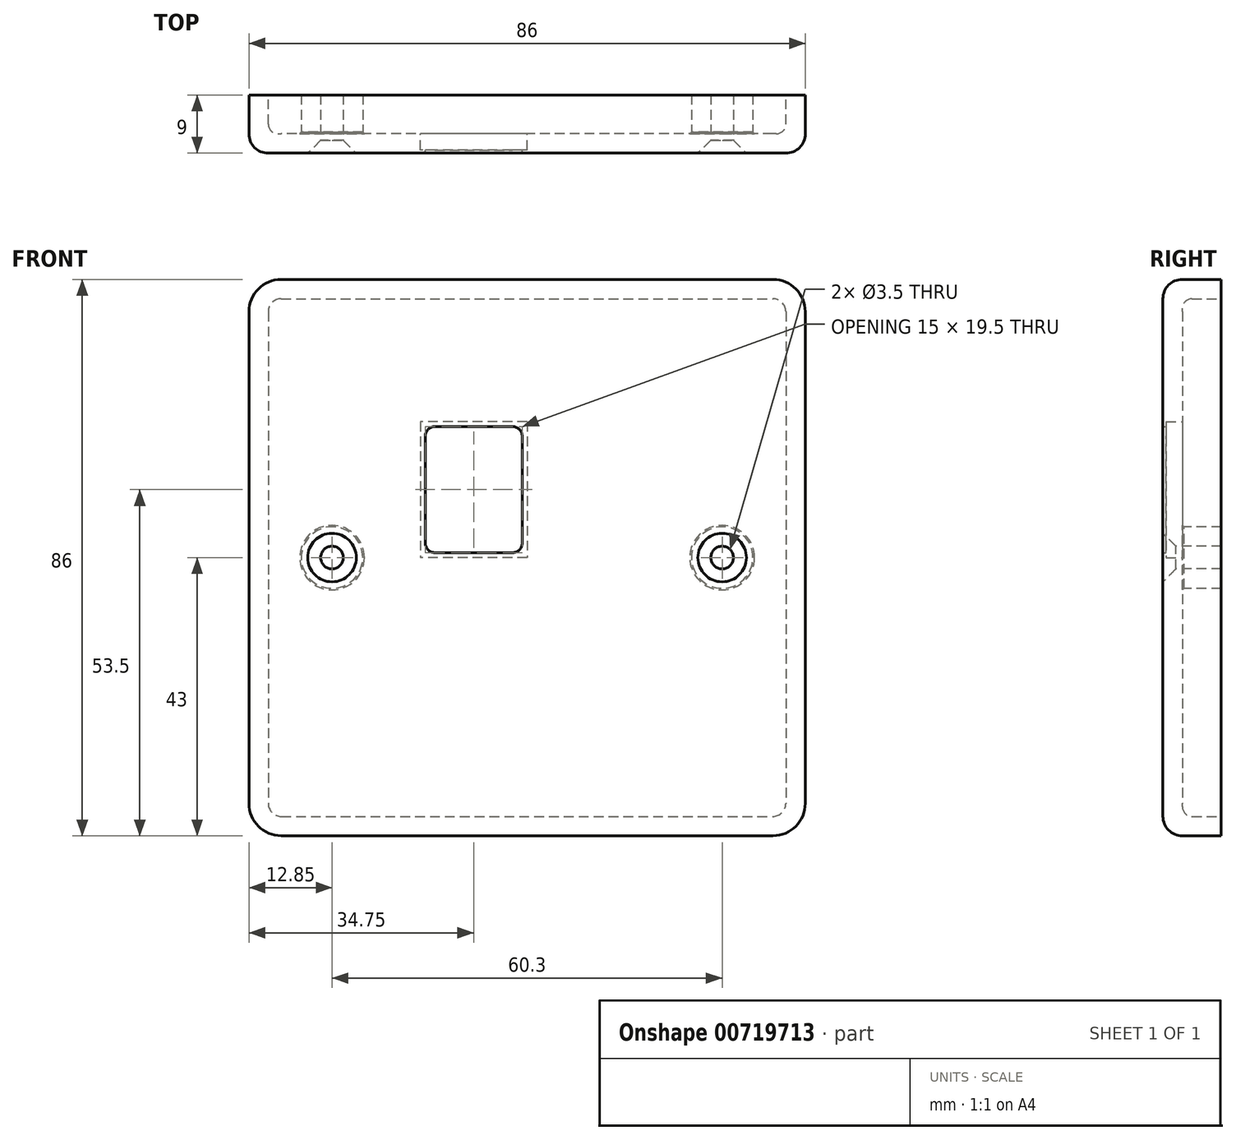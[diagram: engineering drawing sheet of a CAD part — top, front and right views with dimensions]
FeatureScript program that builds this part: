
annotation { "Feature Type Name" : "Feature", "Feature Type Description" : "" }
export const myFeature = defineFeature(function(context is Context, id is Id, definition is map)
    precondition{}
    {
        {
            var Q0;
            Q0=qCreatedBy(makeId("Front.planeOp"),FACE);
            var sketch = newSketch(context, id + "F0", { "sketchPlane" : qUnion([Q0])});
            skLineSegment(sketch, "E0.bottom", {"start": v(-43, 43) * mm, "end": v(43, 43) * mm});
            skLineSegment(sketch, "E0.top", {"start": v(-43, -43) * mm, "end": v(43, -43) * mm});
            skLineSegment(sketch, "E0.left", {"start": v(-43, 43) * mm, "end": v(-43, -43) * mm});
            skLineSegment(sketch, "E0.right", {"start": v(43, 43) * mm, "end": v(43, -43) * mm});
            skPoint(sketch, "E0.middle", {"position": v(0, 0) * mm});
            skSolve(sketch);
        }
        {
            var Q0;
            Q0 = qSketchRegion(id + "F0", true);
            extrude(context, id + "F1", {"entities" : qUnion([Q0]), "depth" : 9 * mm, "offsetDistance" : 25 * mm});
        }
        {
            var Q0;
            Q0=makeQuery(id+"F1.opExtrude","SWEPT_EDGE",EDGE,{"disambiguationData":[OSD([sQuery(id+"F0.wireOp",EDGE,"E0.bottom"),sQuery(id+"F0.wireOp",EDGE,"E0.left")])]});
            var Q1;
            Q1=makeQuery(id+"F1.opExtrude","SWEPT_EDGE",EDGE,{"disambiguationData":[OSD([sQuery(id+"F0.wireOp",EDGE,"E0.bottom"),sQuery(id+"F0.wireOp",EDGE,"E0.right")])]});
            var Q2;
            Q2=makeQuery(id+"F1.opExtrude","SWEPT_EDGE",EDGE,{"disambiguationData":[OSD([sQuery(id+"F0.wireOp",EDGE,"E0.top"),sQuery(id+"F0.wireOp",EDGE,"E0.right")])]});
            var Q3;
            Q3=makeQuery(id+"F1.opExtrude","SWEPT_EDGE",EDGE,{"disambiguationData":[OSD([sQuery(id+"F0.wireOp",EDGE,"E0.top"),sQuery(id+"F0.wireOp",EDGE,"E0.left")])]});
            fillet(context, id + "F2", {"entities" : qUnion([Q0, Q1, Q2, Q3]), "radius" : 5 * mm, "tangentPropagation" : true, "allowEdgeOverflow" : false});
        }
        {
            var Q0;
            Q0=makeQuery(id+"F1.opExtrude","CAP_EDGE",EDGE,{"disambiguationData":[OSD([sQuery(id+"F0.wireOp",EDGE,"E0.right")])],"isStart":false});
            fillet(context, id + "F3", {"entities" : qUnion([Q0]), "radius" : 3 * mm, "tangentPropagation" : true, "allowEdgeOverflow" : false});
        }
        {
            var Q0;
            Q0=makeQuery(id+"F1.opExtrude","CAP_FACE",FACE,{"disambiguationData":[OSD([sQuery(id+"F0.wireOp",EDGE,"E0.bottom"),sQuery(id+"F0.wireOp",EDGE,"E0.top"),sQuery(id+"F0.wireOp",EDGE,"E0.left"),sQuery(id+"F0.wireOp",EDGE,"E0.right")])],"isStart":false});
            var sketch = newSketch(context, id + "F4", { "sketchPlane" : qUnion([Q0])});
            skPoint(sketch, "E1", {"position": v(-30.15, 0) * mm});
            skPoint(sketch, "E2", {"position": v(30.15, 0) * mm});
            skSolve(sketch);
        }
        {
            var Q0;
            Q0=sQuery(id+"F4.wireOp",VERTEX,"E1");
            var Q1;
            Q1=sQuery(id+"F4.wireOp",VERTEX,"E2");
            var Q2;
            Q2=makeQuery(id+"F1.opExtrude","SWEPT_BODY",BODY,{"disambiguationData":[OSD([sQuery(id+"F0.wireOp",EDGE,"E0.bottom"),sQuery(id+"F0.wireOp",EDGE,"E0.top"),sQuery(id+"F0.wireOp",EDGE,"E0.left"),sQuery(id+"F0.wireOp",EDGE,"E0.right")])]});
            hole(context, id + "F5", {"style" : HoleStyle.C_SINK, "endStyle" : HoleEndStyle.THROUGH, "holeDiameter" : 3.5 * mm, "cSinkDiameter" : 7.5 * mm, "cSinkAngle" : 90 * degree, "majorDiameter" : 5 * mm, "isTappedThrough" : true, "tappedDepth" : 12 * mm, "tapClearance" : 3, "locations" : qUnion([Q0, Q1]), "scope" : qUnion([Q2])});
        }
        {
            var Q0;
            Q0=makeQuery(id+"F1.opExtrude","CAP_FACE",FACE,{"disambiguationData":[OSD([sQuery(id+"F0.wireOp",EDGE,"E0.bottom"),sQuery(id+"F0.wireOp",EDGE,"E0.top"),sQuery(id+"F0.wireOp",EDGE,"E0.left"),sQuery(id+"F0.wireOp",EDGE,"E0.right")])],"isStart":true});
            shell(context, id + "F6", {"entities" : qUnion([Q0]), "thickness" : 3 * mm});
        }
        {
            var Q0;
            {var subQ0=sQuery(id+"F0.wireOp",EDGE,"E0.right");var subQ1=sQuery(id+"F0.wireOp",EDGE,"E0.left");var subQ2=sQuery(id+"F0.wireOp",EDGE,"E0.top");var subQ3=sQuery(id+"F0.wireOp",EDGE,"E0.bottom");var subQ4=makeQuery(id+"F1.opExtrude","CAP_EDGE",EDGE,{"disambiguationData":[OSD([subQ3])],"isStart":false});Q0=makeQuery(id+"F6.opShell","OFFSET_EDGE",EDGE,{"disambiguationData":[OSD([subQ3,subQ2,subQ1,subQ0]),TDD([makeQuery(id+"F3.opFillet","BLEND_EDGE",EDGE,{"blendedFrom":[subQ4,makeQuery(id+"F1.opExtrude","SWEPT_FACE",FACE,{"disambiguationData":[OSD([subQ3])]})],"blendedInto":[makeQuery(id+"F1.opExtrude","SWEPT_FACE",FACE,{"disambiguationData":[OSD([subQ3])]})]}),makeQuery(id+"F3.opFillet","BLEND_EDGE",EDGE,{"blendedFrom":[subQ4,makeQuery(id+"F1.opExtrude","CAP_FACE",FACE,{"disambiguationData":[OSD([subQ3,subQ2,subQ1,subQ0])],"isStart":false})],"blendedInto":[makeQuery(id+"F1.opExtrude","CAP_FACE",FACE,{"disambiguationData":[OSD([subQ3,subQ2,subQ1,subQ0])],"isStart":false})]})])]});}
            var Q1;
            Q1=makeQuery(id+"F6.opShell","OFFSET_EDGE",EDGE,{"disambiguationData":[OSD([sQuery(id+"F5.hole-1.sketch.wireOp",EDGE,"csink_start_line_1"),sQuery(id+"F5.hole-1.sketch.wireOp",EDGE,"csink_start_line_2")])]});
            var Q2;
            Q2=makeQuery(id+"F6.opShell","OFFSET_EDGE",EDGE,{"disambiguationData":[OSD([sQuery(id+"F5.hole-0.sketch.wireOp",EDGE,"csink_start_line_1"),sQuery(id+"F5.hole-0.sketch.wireOp",EDGE,"csink_start_line_2")])]});
            fillet(context, id + "F7", {"entities" : qUnion([Q0, Q1, Q2]), "radius" : 1.5 * mm, "tangentPropagation" : true, "allowEdgeOverflow" : false});
        }
        {
            var Q0;
            {var subQ0=sQuery(id+"F0.wireOp",EDGE,"E0.right");var subQ1=sQuery(id+"F0.wireOp",EDGE,"E0.left");var subQ2=sQuery(id+"F0.wireOp",EDGE,"E0.top");var subQ3=sQuery(id+"F0.wireOp",EDGE,"E0.bottom");Q0=makeQuery(id+"F6.opShell","OFFSET_FACE",FACE,{"disambiguationData":[OSD([subQ3,subQ2,subQ1,subQ0]),TDD([makeQuery(id+"F1.opExtrude","CAP_FACE",FACE,{"disambiguationData":[OSD([subQ3,subQ2,subQ1,subQ0])],"isStart":false})])]});}
            var sketch = newSketch(context, id + "F8", { "sketchPlane" : qUnion([Q0])});
            skLineSegment(sketch, "E3.bottom", {"start": v(0, 21) * mm, "end": v(16.5, 21) * mm});
            skLineSegment(sketch, "E3.top", {"start": v(0, 0) * mm, "end": v(16.5, 0) * mm});
            skLineSegment(sketch, "E3.left", {"start": v(0, 21) * mm, "end": v(0, 0) * mm});
            skLineSegment(sketch, "E3.right", {"start": v(16.5, 21) * mm, "end": v(16.5, 0) * mm});
            skSolve(sketch);
        }
        {
            var Q0;
            Q0 = qSketchRegion(id + "F8", true);
            extrude(context, id + "F9", {"entities" : qUnion([Q0]), "operationType" : NewBodyOperationType.REMOVE, "oppositeDirection" : true, "depth" : 2.5 * mm, "offsetDistance" : 25 * mm});
        }
        {
            var Q0;
            Q0=makeQuery(id+"F9.boolean.opBoolean","COPY",FACE,{"derivedFrom":makeQuery(id+"F9.opExtrude","CAP_FACE",FACE,{"disambiguationData":[OSD([sQuery(id+"F8.wireOp",EDGE,"E3.bottom"),sQuery(id+"F8.wireOp",EDGE,"E3.top"),sQuery(id+"F8.wireOp",EDGE,"E3.left"),sQuery(id+"F8.wireOp",EDGE,"E3.right")])],"isStart":false})});
            var sketch = newSketch(context, id + "F10", { "sketchPlane" : qUnion([Q0])});
            skLineSegment(sketch, "E4.bottom", {"start": v(14.25, 0.75) * mm, "end": v(2.25, 0.75) * mm});
            skLineSegment(sketch, "E4.top", {"start": v(14.25, 20.25) * mm, "end": v(2.25, 20.25) * mm});
            skLineSegment(sketch, "E4.left", {"start": v(15.75, 2.25) * mm, "end": v(15.75, 18.75) * mm});
            skLineSegment(sketch, "E4.right", {"start": v(0.75, 2.25) * mm, "end": v(0.75, 18.75) * mm});
            skPoint(sketch, "E4.middle", {"position": v(8.25, 10.5) * mm});
            skPoint(sketch, "E4.middle.positionSnap0", {"position": v(0, 10.5) * mm});
            skPoint(sketch, "E4.middle.positionSnap1", {"position": v(8.25, 21) * mm});
            skPoint(sketch, "E4.centerSnap0", {"position": v(0, 10.5) * mm});
            skPoint(sketch, "E4.centerSnap1", {"position": v(8.25, 21) * mm});
            skPoint(sketch, "E5.visualSharp", {"position": v(0.75, 20.25) * mm});
            skArc(sketch, "E5.filletArc", {"start": v(2.25, 20.25) * mm, "mid": v(1.19, 19.81) * mm, "end": v(0.75, 18.75) * mm});
            skPoint(sketch, "E6.visualSharp", {"position": v(15.75, 20.25) * mm});
            skArc(sketch, "E6.filletArc", {"start": v(15.75, 18.75) * mm, "mid": v(15.31, 19.81) * mm, "end": v(14.25, 20.25) * mm});
            skPoint(sketch, "E7.visualSharp", {"position": v(15.75, 0.75) * mm});
            skArc(sketch, "E7.filletArc", {"start": v(14.25, 0.75) * mm, "mid": v(15.31, 1.19) * mm, "end": v(15.75, 2.25) * mm});
            skPoint(sketch, "E8.visualSharp", {"position": v(0.75, 0.75) * mm});
            skArc(sketch, "E8.filletArc", {"start": v(0.75, 2.25) * mm, "mid": v(1.19, 1.19) * mm, "end": v(2.25, 0.75) * mm});
            skSolve(sketch);
        }
        {
            var Q0;
            Q0 = qSketchRegion(id + "F10", true);
            extrude(context, id + "F11", {"entities" : qUnion([Q0]), "operationType" : NewBodyOperationType.REMOVE, "endBound" : BoundingType.UP_TO_NEXT, "oppositeDirection" : true, "depth" : 25 * mm, "offsetDistance" : 25 * mm});
        }
    });
